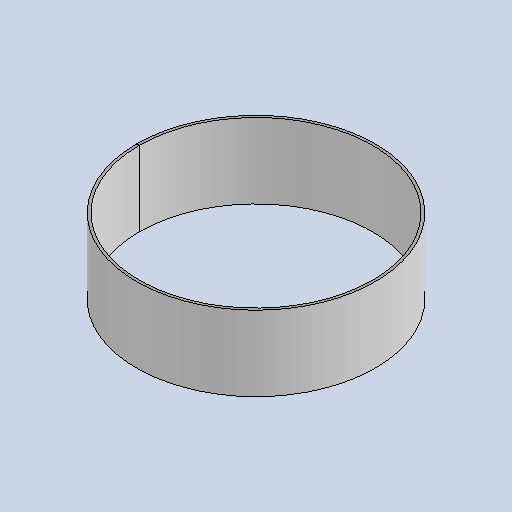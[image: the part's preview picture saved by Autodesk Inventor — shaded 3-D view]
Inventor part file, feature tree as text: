
AUTODESK INVENTOR PART (.ipt)
format: ipt  version: 2025.1 (Build 291241020, 241B)  size: 138,752 bytes
history: native  units: mm
features: sketch x2, revolve x1, extrude x1, other x1
ambient origin geometry x8: Origin, YZ Plane, XZ Plane, XY Plane, X Axis, Y Axis, Z Axis, Center Point
bodies: Solid1 (feature_tree)
feature tree (5):
  revolve  "Revolution1"  [1 undecoded]
  extrude  "Extrusion1"  Depth=62.8144mm
  sketch  "Sketch1"  dims[d1=6.0mm d3=6.0mm d4=530.0mm]
  sketch  "Sketch2"  dims[d5=120.0mm d6=62.8144mm d7=6.0mm d8=50.0mm d9=952.0mm d10=0.0mm d11=0.0mm]
  other  "Definition1"
note: 1 required parameter value undecoded (feature->parameter linkage not recoverable at this tier; creation-order binding heuristic only, values carry confidence <= 0.55)
